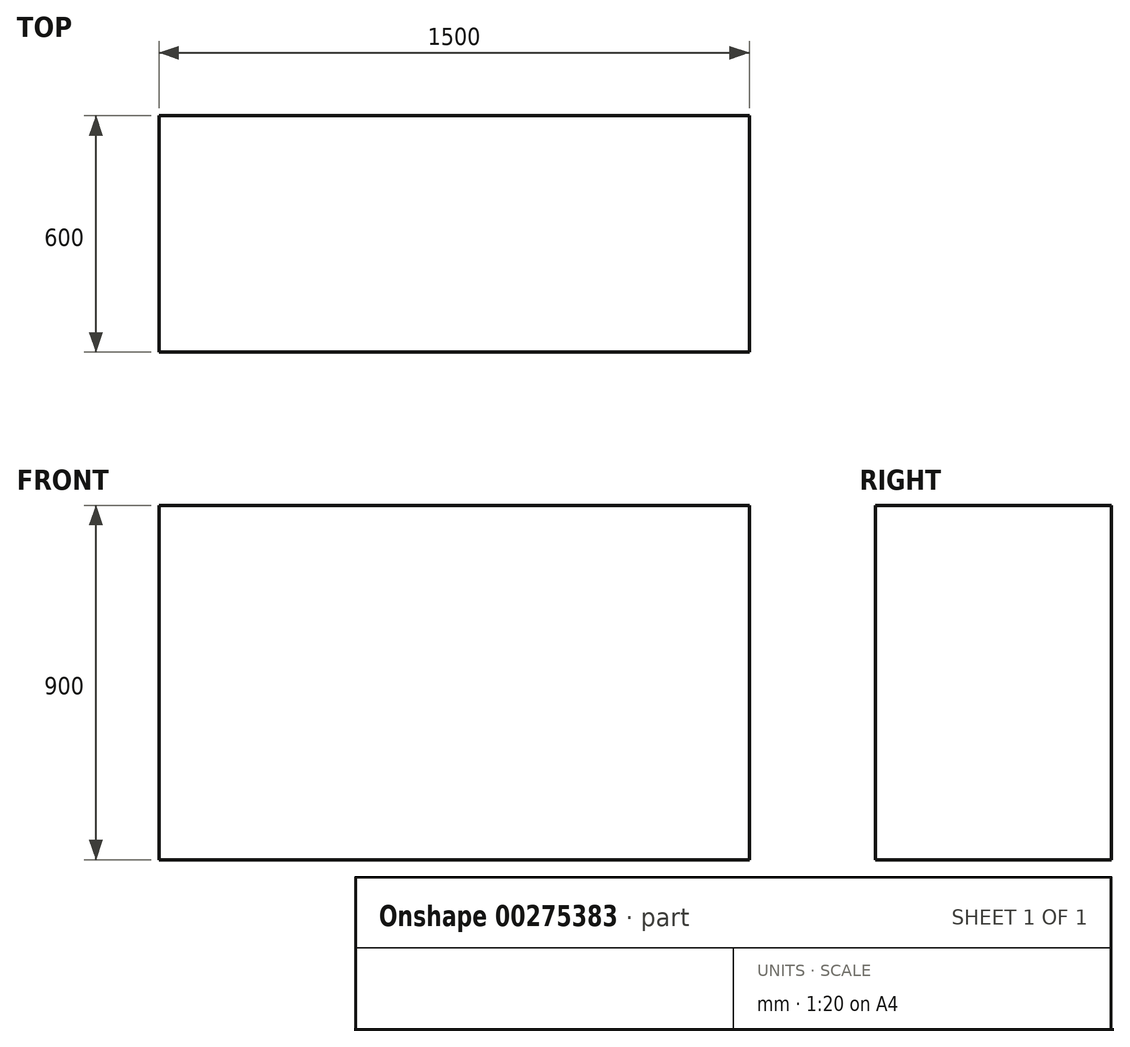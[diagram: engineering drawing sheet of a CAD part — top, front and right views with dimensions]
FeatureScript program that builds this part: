
annotation { "Feature Type Name" : "Feature", "Feature Type Description" : "" }
export const myFeature = defineFeature(function(context is Context, id is Id, definition is map)
    precondition{}
    {
        {
            var Q0;
            Q0=qCreatedBy(makeId("Top.planeOp"),FACE);
            var sketch = newSketch(context, id + "F0", { "sketchPlane" : qUnion([Q0])});
            skLineSegment(sketch, "E0.bottom", {"start": v(-750, 300) * mm, "end": v(750, 300) * mm});
            skLineSegment(sketch, "E0.top", {"start": v(-750, -300) * mm, "end": v(750, -300) * mm});
            skLineSegment(sketch, "E0.left", {"start": v(-750, 300) * mm, "end": v(-750, -300) * mm});
            skLineSegment(sketch, "E0.right", {"start": v(750, 300) * mm, "end": v(750, -300) * mm});
            skPoint(sketch, "E0.middle", {"position": v(0, 0) * mm});
            skSolve(sketch);
        }
        {
            var Q0;
            Q0 = qSketchRegion(id + "F0", true);
            extrude(context, id + "F1", {"entities" : qUnion([Q0]), "depth" : 900 * mm, "offsetDistance" : 25 * mm});
        }
    });
